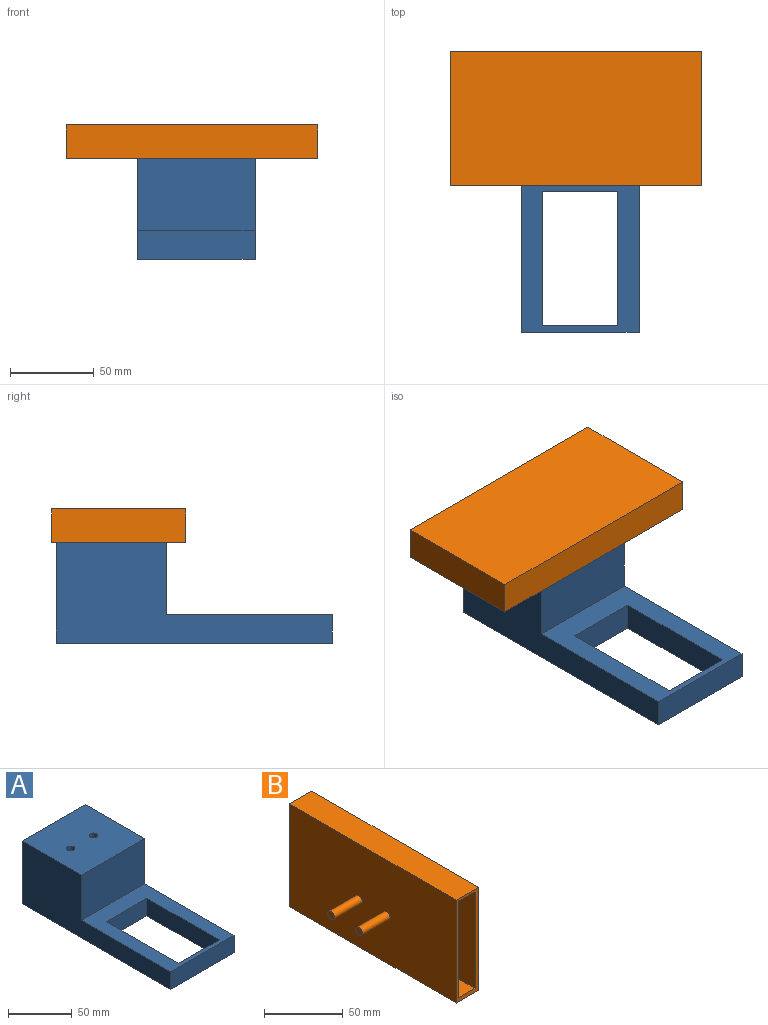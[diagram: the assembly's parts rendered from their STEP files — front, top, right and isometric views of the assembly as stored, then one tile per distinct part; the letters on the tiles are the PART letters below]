
ASSEMBLY  parts=2 mates=1
PART A: 16 faces, bbox 70x164.6x60 mm
  f0: plane 164.6x70mm, normal (0,0,-1), area 7922mm2, adj f4,f5,f6,f11,f12,f13,f14,f15
  f1: plane 99.1x70mm, normal (0,0,1), area 3337mm2, adj f2,f4,f5,f11,f12,f13,f14,f15
  f2: plane 70x43.19mm, normal (0,-1,0), area 3023.2mm2, adj f1,f3,f4,f5
  f3: plane 70x65.5mm, normal (0,0,1), area 4518.6mm2, adj f2,f4,f5,f6,f7,f9
  f4: plane 164.6x60mm, normal (-1,0,0), area 5596mm2, adj f0,f1,f2,f3,f6,f11
  f5: plane 164.6x60mm, normal (1,0,0), area 5596mm2, adj f0,f1,f2,f3,f6,f11
  f6: plane 70x60mm, normal (0,1,0), area 4200mm2, adj f0,f3,f4,f5
  f7: cylinder r=3.25mm len=25mm, axis (0,0,1), area 510.5mm2, adj f3,f8
  f8: plane 6.5x6.5mm, normal (0,0,1), area 33.2mm2, adj f7
  f9: cylinder r=3.25mm len=25mm, axis (0,0,1), area 510.5mm2, adj f3,f10
  f10: plane 6.5x6.5mm, normal (0,0,1), area 33.2mm2, adj f9
  f11: plane 70x16.81mm, normal (0,-1,0), area 1176.8mm2, adj f0,f1,f4,f5
  f12: plane 45x16.81mm, normal (0,-1,0), area 756.5mm2, adj f0,f1,f13,f15
  f13: plane 80x16.81mm, normal (1,0,0), area 1344.9mm2, adj f0,f1,f12,f14
  f14: plane 45x16.81mm, normal (0,1,0), area 756.5mm2, adj f0,f1,f13,f15
  f15: plane 80x16.81mm, normal (-1,0,0), area 1344.9mm2, adj f0,f1,f12,f14
PART B: 15 faces, bbox 45x150x80 mm
  f0: plane 80x20mm, normal (0,-1,0), area 486.2mm2, adj f1,f2,f3,f4,f6,f7,f8,f9
  f1: plane 150x20mm, normal (0,0,1), area 3000mm2, adj f0,f2,f4,f5
  f2: plane 150x80mm, normal (-1,0,0), area 11943.5mm2, adj f0,f1,f3,f5,f11,f13
  f3: plane 150x20mm, normal (0,0,-1), area 3000mm2, adj f0,f2,f4,f5
  f4: plane 150x80mm, normal (1,0,0), area 12000mm2, adj f0,f1,f3,f5
  f5: plane 80x20mm, normal (0,1,0), area 1600mm2, adj f1,f2,f3,f4
  f6: plane 148.9x14.85mm, normal (0,0,-1), area 2211.2mm2, adj f0,f7,f9,f10
  f7: plane 148.9x75mm, normal (1,0,0), area 11167.5mm2, adj f0,f6,f8,f10
  f8: plane 148.9x14.85mm, normal (0,0,1), area 2211.2mm2, adj f0,f7,f9,f10
  f9: plane 148.9x75mm, normal (-1,0,0), area 11167.5mm2, adj f0,f6,f8,f10
  f10: plane 75x14.85mm, normal (0,-1,0), area 1113.8mm2, adj f6,f7,f8,f9
  f11: cylinder r=3mm len=25mm, axis (1,0,0), area 471.2mm2, adj f2,f12
  f12: plane 6x6mm, normal (-1,0,0), area 28.3mm2, adj f11
  f13: cylinder r=3mm len=25mm, axis (1,0,0), area 471.2mm2, adj f2,f14
  f14: plane 6x6mm, normal (-1,0,0), area 28.3mm2, adj f13
PLACE A t=(-37.15,2.24,11.46)mm
PLACE B rot(axis=(0.58,-0.58,0.58),120deg) t=(-112.15,-31.89,92.21)mm
MATE fastened B.f13 <-> A.f9  axis (0,0,-1) through (-24.65,-31.89,12.14)mm
